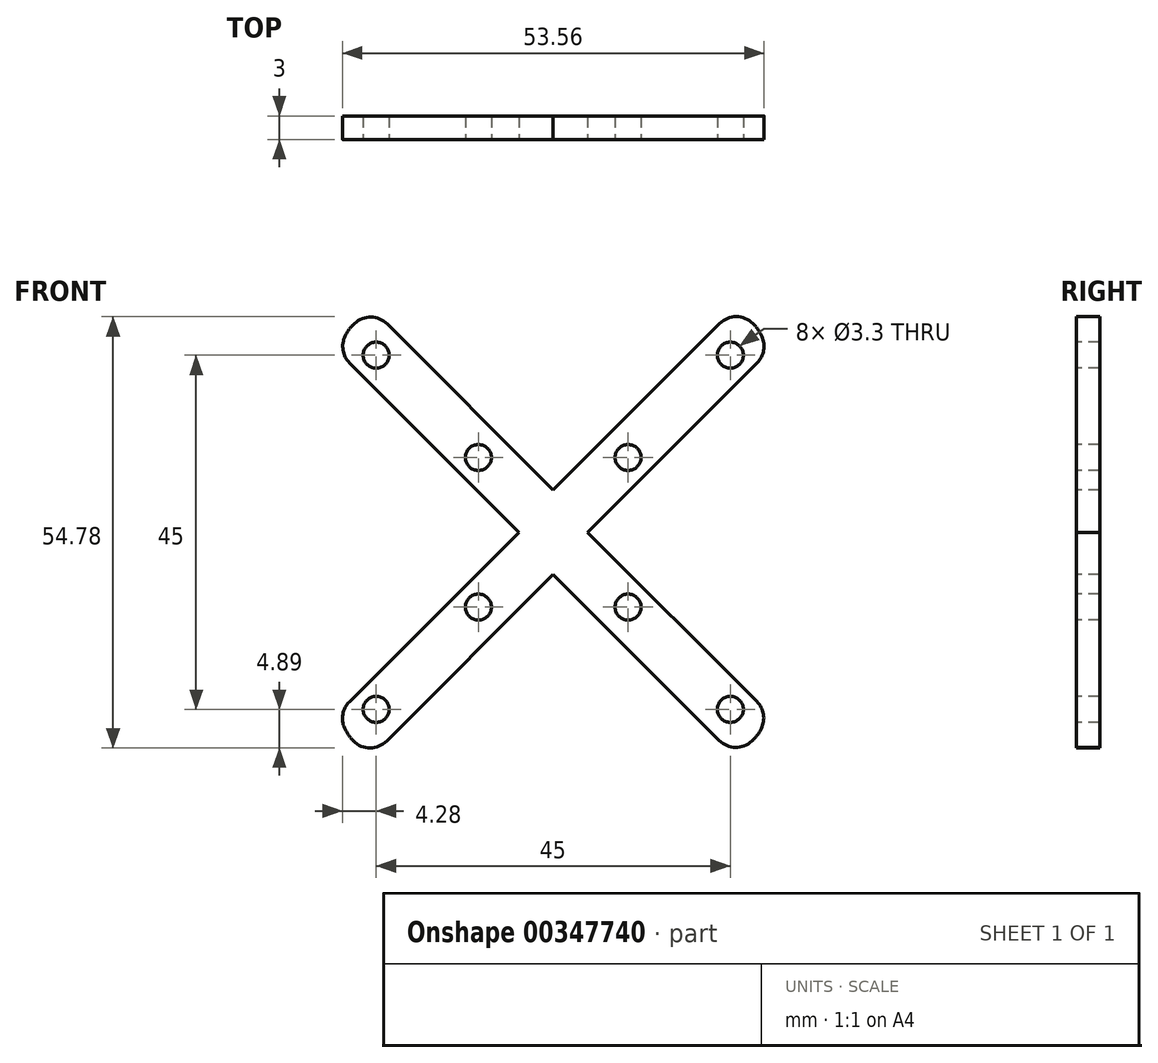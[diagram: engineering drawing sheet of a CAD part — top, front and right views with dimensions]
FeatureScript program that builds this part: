
annotation { "Feature Type Name" : "Feature", "Feature Type Description" : "" }
export const myFeature = defineFeature(function(context is Context, id is Id, definition is map)
    precondition{}
    {
        {
            var Q0;
            Q0=qCreatedBy(makeId("Front.planeOp"),FACE);
            var sketch = newSketch(context, id + "F0", { "sketchPlane" : qUnion([Q0])});
            skLineSegment(sketch, "E0.bottom", {"start": v(27, -28) * mm, "end": v(-27, -28) * mm});
            skLineSegment(sketch, "E0.top", {"start": v(27, 28) * mm, "end": v(-27, 28) * mm});
            skLineSegment(sketch, "E0.left", {"start": v(27, -28) * mm, "end": v(27, 28) * mm});
            skLineSegment(sketch, "E0.right", {"start": v(-27, -28) * mm, "end": v(-27, 28) * mm});
            skPoint(sketch, "E0.middle", {"position": v(0, 0) * mm});
            skSolve(sketch);
        }
        {
            var Q0;
            Q0 = qSketchRegion(id + "F0", true);
            extrude(context, id + "F1", {"entities" : qUnion([Q0]), "depth" : 3 * mm});
        }
        {
            var Q0;
            Q0=makeQuery(id+"F1.opExtrude","CAP_FACE",FACE,{"disambiguationData":[OSD([sQuery(id+"F0.wireOp",EDGE,"E0.bottom"),sQuery(id+"F0.wireOp",EDGE,"E0.top"),sQuery(id+"F0.wireOp",EDGE,"E0.left"),sQuery(id+"F0.wireOp",EDGE,"E0.right")])],"isStart":false});
            var sketch = newSketch(context, id + "F2", { "sketchPlane" : qUnion([Q0])});
            skLineSegment(sketch, "E1.bottom", {"start": v(22.5, -22.5) * mm, "end": v(-22.5, -22.5) * mm, "construction": true});
            skLineSegment(sketch, "E1.top", {"start": v(22.5, 22.5) * mm, "end": v(-22.5, 22.5) * mm, "construction": true});
            skLineSegment(sketch, "E1.left", {"start": v(22.5, -22.5) * mm, "end": v(22.5, 22.5) * mm, "construction": true});
            skLineSegment(sketch, "E1.right", {"start": v(-22.5, -22.5) * mm, "end": v(-22.5, 22.5) * mm, "construction": true});
            skPoint(sketch, "E1.middle", {"position": v(0, 0) * mm});
            skCircle(sketch, "E2", {"center": v(-22.5, 22.5) * mm, "radius": 2.63 * mm});
            skCircle(sketch, "E3", {"center": v(22.5, 22.5) * mm, "radius": 2.72 * mm});
            skCircle(sketch, "E4", {"center": v(-22.5, -22.5) * mm, "radius": 1.67 * mm});
            skCircle(sketch, "E5", {"center": v(22.5, -22.5) * mm, "radius": 2.13 * mm});
            skSolve(sketch);
        }
        {
            var Q0;
            Q0=sQuery(id+"F2.wireOp",VERTEX,"E1.top.end");
            var Q1;
            Q1=sQuery(id+"F2.wireOp",VERTEX,"E1.left.end");
            var Q2;
            Q2=sQuery(id+"F2.wireOp",VERTEX,"E1.left.start");
            var Q3;
            Q3=sQuery(id+"F2.wireOp",VERTEX,"E1.right.start");
            var Q4;
            Q4=makeQuery(id+"F1.opExtrude","SWEPT_BODY",BODY,{"disambiguationData":[OSD([sQuery(id+"F0.wireOp",EDGE,"E0.bottom"),sQuery(id+"F0.wireOp",EDGE,"E0.top"),sQuery(id+"F0.wireOp",EDGE,"E0.left"),sQuery(id+"F0.wireOp",EDGE,"E0.right")])]});
            hole(context, id + "F3", {"style" : HoleStyle.SIMPLE, "endStyle" : HoleEndStyle.BLIND, "standardTappedOrClearance" : lookupTablePath({ "standard" : "ISO", "fit" : "Normal", "size" : "M3", "type" : "Clearance" }), "standardBlindInLast" : lookupTablePath({ "fit" : "Standard", "standard" : "ISO", "size" : "M3", "type" : "Clearance" }), "holeDiameter" : 3.3 * mm, "holeDepth" : 4.55 * mm, "isTappedThrough" : true, "tappedDepth" : 2.75 * mm, "tapClearance" : 3, "startFromSketch" : true, "locations" : qUnion([Q0, Q1, Q2, Q3]), "scope" : qUnion([Q4])});
        }
        {
            var Q0;
            Q0=makeQuery(id+"F1.opExtrude","CAP_FACE",FACE,{"disambiguationData":[OSD([sQuery(id+"F0.wireOp",EDGE,"E0.bottom"),sQuery(id+"F0.wireOp",EDGE,"E0.top"),sQuery(id+"F0.wireOp",EDGE,"E0.left"),sQuery(id+"F0.wireOp",EDGE,"E0.right")])],"isStart":false});
            var sketch = newSketch(context, id + "F4", { "sketchPlane" : qUnion([Q0])});
            skLineSegment(sketch, "E6.bottom", {"start": v(-22.63, 28) * mm, "end": v(0, 5.37) * mm});
            skLineSegment(sketch, "E6.top", {"start": v(0, 50.63) * mm, "end": v(22.63, 28) * mm});
            skLineSegment(sketch, "E6.left", {"start": v(-22.63, 28) * mm, "end": v(0, 50.63) * mm});
            skLineSegment(sketch, "E6.right", {"start": v(0, 5.37) * mm, "end": v(22.63, 28) * mm});
            skPoint(sketch, "E6.middle", {"position": v(0, 28) * mm});
            skLineSegment(sketch, "E7.bottom", {"start": v(-49.63, 0) * mm, "end": v(-27, 22.63) * mm});
            skLineSegment(sketch, "E7.top", {"start": v(-27, -22.63) * mm, "end": v(-4.37, 0) * mm});
            skLineSegment(sketch, "E7.left", {"start": v(-49.63, 0) * mm, "end": v(-27, -22.63) * mm});
            skLineSegment(sketch, "E7.right", {"start": v(-27, 22.63) * mm, "end": v(-4.37, 0) * mm});
            skPoint(sketch, "E7.middle", {"position": v(-27, 0) * mm});
            skLineSegment(sketch, "E8.bottom", {"start": v(-22.63, -28) * mm, "end": v(0, -5.37) * mm});
            skLineSegment(sketch, "E8.top", {"start": v(0, -50.63) * mm, "end": v(22.63, -28) * mm});
            skLineSegment(sketch, "E8.left", {"start": v(-22.63, -28) * mm, "end": v(0, -50.63) * mm});
            skLineSegment(sketch, "E8.right", {"start": v(0, -5.37) * mm, "end": v(22.63, -28) * mm});
            skPoint(sketch, "E8.middle", {"position": v(0, -28) * mm});
            skLineSegment(sketch, "E9.bottom", {"start": v(27, -22.63) * mm, "end": v(49.63, 0) * mm});
            skLineSegment(sketch, "E9.top", {"start": v(4.37, 0) * mm, "end": v(27, 22.63) * mm});
            skLineSegment(sketch, "E9.left", {"start": v(27, -22.63) * mm, "end": v(4.37, 0) * mm});
            skLineSegment(sketch, "E9.right", {"start": v(49.63, 0) * mm, "end": v(27, 22.63) * mm});
            skPoint(sketch, "E9.middle", {"position": v(27, 0) * mm});
            skSolve(sketch);
        }
        {
            var Q0;
            {var subQ0=sQuery(id+"F4.wireOp",EDGE,"E7.top");Q0=makeQuery(id+"F4.imprint","IMPRINT",FACE,{"disambiguationData":[TD([[makeQuery(id+"F4.imprint","IMPRINT",EDGE,{"derivedFrom":subQ0}),1.0]])]});}
            var Q1;
            {var subQ0=sQuery(id+"F4.wireOp",EDGE,"E6.bottom");Q1=makeQuery(id+"F4.imprint","IMPRINT",FACE,{"disambiguationData":[TD([[makeQuery(id+"F4.imprint","IMPRINT",EDGE,{"derivedFrom":subQ0}),1.0]])]});}
            var Q2;
            {var subQ0=sQuery(id+"F4.wireOp",EDGE,"E9.top");Q2=makeQuery(id+"F4.imprint","IMPRINT",FACE,{"disambiguationData":[TD([[makeQuery(id+"F4.imprint","IMPRINT",EDGE,{"derivedFrom":subQ0}),-1.0]])]});}
            var Q3;
            {var subQ0=sQuery(id+"F4.wireOp",EDGE,"E8.bottom");Q3=makeQuery(id+"F4.imprint","IMPRINT",FACE,{"disambiguationData":[TD([[makeQuery(id+"F4.imprint","IMPRINT",EDGE,{"derivedFrom":subQ0}),-1.0]])]});}
            extrude(context, id + "F5", {"entities" : qUnion([Q0, Q1, Q2, Q3]), "operationType" : NewBodyOperationType.REMOVE, "endBound" : BoundingType.THROUGH_ALL, "oppositeDirection" : true, "depth" : 25 * mm});
        }
        {
            var Q0;
            Q0=makeQuery(id+"F1.opExtrude","CAP_FACE",FACE,{"disambiguationData":[OSD([sQuery(id+"F0.wireOp",EDGE,"E0.bottom"),sQuery(id+"F0.wireOp",EDGE,"E0.top"),sQuery(id+"F0.wireOp",EDGE,"E0.left"),sQuery(id+"F0.wireOp",EDGE,"E0.right")])],"isStart":false});
            var sketch = newSketch(context, id + "F6", { "sketchPlane" : qUnion([Q0])});
            skLineSegment(sketch, "E10.bottom", {"start": v(-9.5, 9.5) * mm, "end": v(9.5, 9.5) * mm, "construction": true});
            skLineSegment(sketch, "E10.top", {"start": v(-9.5, -9.5) * mm, "end": v(9.5, -9.5) * mm, "construction": true});
            skLineSegment(sketch, "E10.left", {"start": v(-9.5, 9.5) * mm, "end": v(-9.5, -9.5) * mm, "construction": true});
            skLineSegment(sketch, "E10.right", {"start": v(9.5, 9.5) * mm, "end": v(9.5, -9.5) * mm, "construction": true});
            skPoint(sketch, "E10.middle", {"position": v(0, 0) * mm});
            skPoint(sketch, "E10.cornerSnap0", {"position": v(-9.5, 24.88) * mm});
            skCircle(sketch, "E11", {"center": v(-9.5, 9.5) * mm, "radius": 1.62 * mm});
            skCircle(sketch, "E12", {"center": v(9.5, 9.5) * mm, "radius": 2.08 * mm});
            skCircle(sketch, "E13", {"center": v(9.5, -9.5) * mm, "radius": 1.98 * mm});
            skCircle(sketch, "E14", {"center": v(-9.5, -9.5) * mm, "radius": 2.43 * mm});
            skSolve(sketch);
        }
        {
            var Q0;
            Q0=sQuery(id+"F6.wireOp",VERTEX,"E11.center");
            var Q1;
            Q1=sQuery(id+"F6.wireOp",VERTEX,"E12.center");
            var Q2;
            Q2=sQuery(id+"F6.wireOp",VERTEX,"E13.center");
            var Q3;
            Q3=sQuery(id+"F6.wireOp",VERTEX,"E10.left.end");
            var Q4;
            Q4=makeQuery(id+"F1.opExtrude","SWEPT_BODY",BODY,{"disambiguationData":[OSD([sQuery(id+"F0.wireOp",EDGE,"E0.bottom"),sQuery(id+"F0.wireOp",EDGE,"E0.top"),sQuery(id+"F0.wireOp",EDGE,"E0.left"),sQuery(id+"F0.wireOp",EDGE,"E0.right")])]});
            hole(context, id + "F7", {"style" : HoleStyle.SIMPLE, "endStyle" : HoleEndStyle.BLIND, "standardTappedOrClearance" : lookupTablePath({ "standard" : "ISO", "fit" : "Normal", "size" : "M3", "type" : "Clearance" }), "standardBlindInLast" : lookupTablePath({ "fit" : "Standard", "standard" : "ISO", "size" : "M3", "type" : "Clearance" }), "holeDiameter" : 3.3 * mm, "holeDepth" : 4.55 * mm, "isTappedThrough" : true, "tappedDepth" : 2.75 * mm, "tapClearance" : 3, "startFromSketch" : true, "locations" : qUnion([Q0, Q1, Q2, Q3]), "scope" : qUnion([Q4])});
        }
        {
            var Q0;
            Q0=makeQuery(id+"F1.opExtrude","SWEPT_EDGE",EDGE,{"disambiguationData":[OSD([sQuery(id+"F0.wireOp",EDGE,"E0.top"),sQuery(id+"F0.wireOp",EDGE,"E0.right")])]});
            var Q1;
            Q1=makeQuery(id+"F1.opExtrude","SWEPT_EDGE",EDGE,{"disambiguationData":[OSD([sQuery(id+"F0.wireOp",EDGE,"E0.top"),sQuery(id+"F0.wireOp",EDGE,"E0.left")])]});
            var Q2;
            Q2=makeQuery(id+"F1.opExtrude","SWEPT_EDGE",EDGE,{"disambiguationData":[OSD([sQuery(id+"F0.wireOp",EDGE,"E0.bottom"),sQuery(id+"F0.wireOp",EDGE,"E0.left")])]});
            var Q3;
            Q3=makeQuery(id+"F1.opExtrude","SWEPT_EDGE",EDGE,{"disambiguationData":[OSD([sQuery(id+"F0.wireOp",EDGE,"E0.bottom"),sQuery(id+"F0.wireOp",EDGE,"E0.right")])]});
            fillet(context, id + "F8", {"entities" : qUnion([Q0, Q1, Q2, Q3]), "radius" : 5.5 * mm, "tangentPropagation" : true, "allowEdgeOverflow" : false});
        }
        {
            var Q0;
            Q0=makeQuery(id+"F8.opFillet","BLEND_EDGE",EDGE,{"blendedFrom":[makeQuery(id+"F1.opExtrude","SWEPT_EDGE",EDGE,{"disambiguationData":[OSD([sQuery(id+"F0.wireOp",EDGE,"E0.top"),sQuery(id+"F0.wireOp",EDGE,"E0.right")])]}),makeQuery(id+"F5.boolean.opBoolean","COPY",FACE,{"derivedFrom":makeQuery(id+"F5.opExtrude","SWEPT_FACE",FACE,{"disambiguationData":[OSD([sQuery(id+"F4.wireOp",EDGE,"E7.right")])]})})],"blendedInto":[makeQuery(id+"F5.boolean.opBoolean","COPY",FACE,{"derivedFrom":makeQuery(id+"F5.opExtrude","SWEPT_FACE",FACE,{"disambiguationData":[OSD([sQuery(id+"F4.wireOp",EDGE,"E7.right")])]})})]});
            var Q1;
            Q1=makeQuery(id+"F8.opFillet","BLEND_EDGE",EDGE,{"blendedFrom":[makeQuery(id+"F1.opExtrude","SWEPT_EDGE",EDGE,{"disambiguationData":[OSD([sQuery(id+"F0.wireOp",EDGE,"E0.bottom"),sQuery(id+"F0.wireOp",EDGE,"E0.right")])]}),makeQuery(id+"F5.boolean.opBoolean","COPY",FACE,{"derivedFrom":makeQuery(id+"F5.opExtrude","SWEPT_FACE",FACE,{"disambiguationData":[OSD([sQuery(id+"F4.wireOp",EDGE,"E7.top")])]})})],"blendedInto":[makeQuery(id+"F5.boolean.opBoolean","COPY",FACE,{"derivedFrom":makeQuery(id+"F5.opExtrude","SWEPT_FACE",FACE,{"disambiguationData":[OSD([sQuery(id+"F4.wireOp",EDGE,"E7.top")])]})})]});
            var Q2;
            Q2=makeQuery(id+"F8.opFillet","BLEND_EDGE",EDGE,{"blendedFrom":[makeQuery(id+"F1.opExtrude","SWEPT_EDGE",EDGE,{"disambiguationData":[OSD([sQuery(id+"F0.wireOp",EDGE,"E0.bottom"),sQuery(id+"F0.wireOp",EDGE,"E0.left")])]}),makeQuery(id+"F5.boolean.opBoolean","COPY",FACE,{"derivedFrom":makeQuery(id+"F5.opExtrude","SWEPT_FACE",FACE,{"disambiguationData":[OSD([sQuery(id+"F4.wireOp",EDGE,"E9.left")])]})})],"blendedInto":[makeQuery(id+"F5.boolean.opBoolean","COPY",FACE,{"derivedFrom":makeQuery(id+"F5.opExtrude","SWEPT_FACE",FACE,{"disambiguationData":[OSD([sQuery(id+"F4.wireOp",EDGE,"E9.left")])]})})]});
            var Q3;
            Q3=makeQuery(id+"F8.opFillet","BLEND_EDGE",EDGE,{"blendedFrom":[makeQuery(id+"F1.opExtrude","SWEPT_EDGE",EDGE,{"disambiguationData":[OSD([sQuery(id+"F0.wireOp",EDGE,"E0.top"),sQuery(id+"F0.wireOp",EDGE,"E0.left")])]}),makeQuery(id+"F5.boolean.opBoolean","COPY",FACE,{"derivedFrom":makeQuery(id+"F5.opExtrude","SWEPT_FACE",FACE,{"disambiguationData":[OSD([sQuery(id+"F4.wireOp",EDGE,"E9.top")])]})})],"blendedInto":[makeQuery(id+"F5.boolean.opBoolean","COPY",FACE,{"derivedFrom":makeQuery(id+"F5.opExtrude","SWEPT_FACE",FACE,{"disambiguationData":[OSD([sQuery(id+"F4.wireOp",EDGE,"E9.top")])]})})]});
            var Q4;
            Q4=makeQuery(id+"F8.opFillet","BLEND_EDGE",EDGE,{"blendedFrom":[makeQuery(id+"F1.opExtrude","SWEPT_EDGE",EDGE,{"disambiguationData":[OSD([sQuery(id+"F0.wireOp",EDGE,"E0.bottom"),sQuery(id+"F0.wireOp",EDGE,"E0.right")])]}),makeQuery(id+"F5.boolean.opBoolean","COPY",FACE,{"derivedFrom":makeQuery(id+"F5.opExtrude","SWEPT_FACE",FACE,{"disambiguationData":[OSD([sQuery(id+"F4.wireOp",EDGE,"E8.bottom")])]})})],"blendedInto":[makeQuery(id+"F5.boolean.opBoolean","COPY",FACE,{"derivedFrom":makeQuery(id+"F5.opExtrude","SWEPT_FACE",FACE,{"disambiguationData":[OSD([sQuery(id+"F4.wireOp",EDGE,"E8.bottom")])]})})]});
            var Q5;
            Q5=makeQuery(id+"F8.opFillet","BLEND_EDGE",EDGE,{"blendedFrom":[makeQuery(id+"F1.opExtrude","SWEPT_EDGE",EDGE,{"disambiguationData":[OSD([sQuery(id+"F0.wireOp",EDGE,"E0.bottom"),sQuery(id+"F0.wireOp",EDGE,"E0.left")])]}),makeQuery(id+"F5.boolean.opBoolean","COPY",FACE,{"derivedFrom":makeQuery(id+"F5.opExtrude","SWEPT_FACE",FACE,{"disambiguationData":[OSD([sQuery(id+"F4.wireOp",EDGE,"E8.right")])]})})],"blendedInto":[makeQuery(id+"F5.boolean.opBoolean","COPY",FACE,{"derivedFrom":makeQuery(id+"F5.opExtrude","SWEPT_FACE",FACE,{"disambiguationData":[OSD([sQuery(id+"F4.wireOp",EDGE,"E8.right")])]})})]});
            var Q6;
            Q6=makeQuery(id+"F8.opFillet","BLEND_EDGE",EDGE,{"blendedFrom":[makeQuery(id+"F1.opExtrude","SWEPT_EDGE",EDGE,{"disambiguationData":[OSD([sQuery(id+"F0.wireOp",EDGE,"E0.top"),sQuery(id+"F0.wireOp",EDGE,"E0.right")])]}),makeQuery(id+"F5.boolean.opBoolean","COPY",FACE,{"derivedFrom":makeQuery(id+"F5.opExtrude","SWEPT_FACE",FACE,{"disambiguationData":[OSD([sQuery(id+"F4.wireOp",EDGE,"E6.bottom")])]})})],"blendedInto":[makeQuery(id+"F5.boolean.opBoolean","COPY",FACE,{"derivedFrom":makeQuery(id+"F5.opExtrude","SWEPT_FACE",FACE,{"disambiguationData":[OSD([sQuery(id+"F4.wireOp",EDGE,"E6.bottom")])]})})]});
            var Q7;
            Q7=makeQuery(id+"F8.opFillet","BLEND_EDGE",EDGE,{"blendedFrom":[makeQuery(id+"F1.opExtrude","SWEPT_EDGE",EDGE,{"disambiguationData":[OSD([sQuery(id+"F0.wireOp",EDGE,"E0.top"),sQuery(id+"F0.wireOp",EDGE,"E0.left")])]}),makeQuery(id+"F5.boolean.opBoolean","COPY",FACE,{"derivedFrom":makeQuery(id+"F5.opExtrude","SWEPT_FACE",FACE,{"disambiguationData":[OSD([sQuery(id+"F4.wireOp",EDGE,"E6.right")])]})})],"blendedInto":[makeQuery(id+"F5.boolean.opBoolean","COPY",FACE,{"derivedFrom":makeQuery(id+"F5.opExtrude","SWEPT_FACE",FACE,{"disambiguationData":[OSD([sQuery(id+"F4.wireOp",EDGE,"E6.right")])]})})]});
            fillet(context, id + "F9", {"entities" : qUnion([Q0, Q1, Q2, Q3, Q4, Q5, Q6, Q7]), "radius" : 3 * mm, "tangentPropagation" : true, "allowEdgeOverflow" : false});
        }
    });
